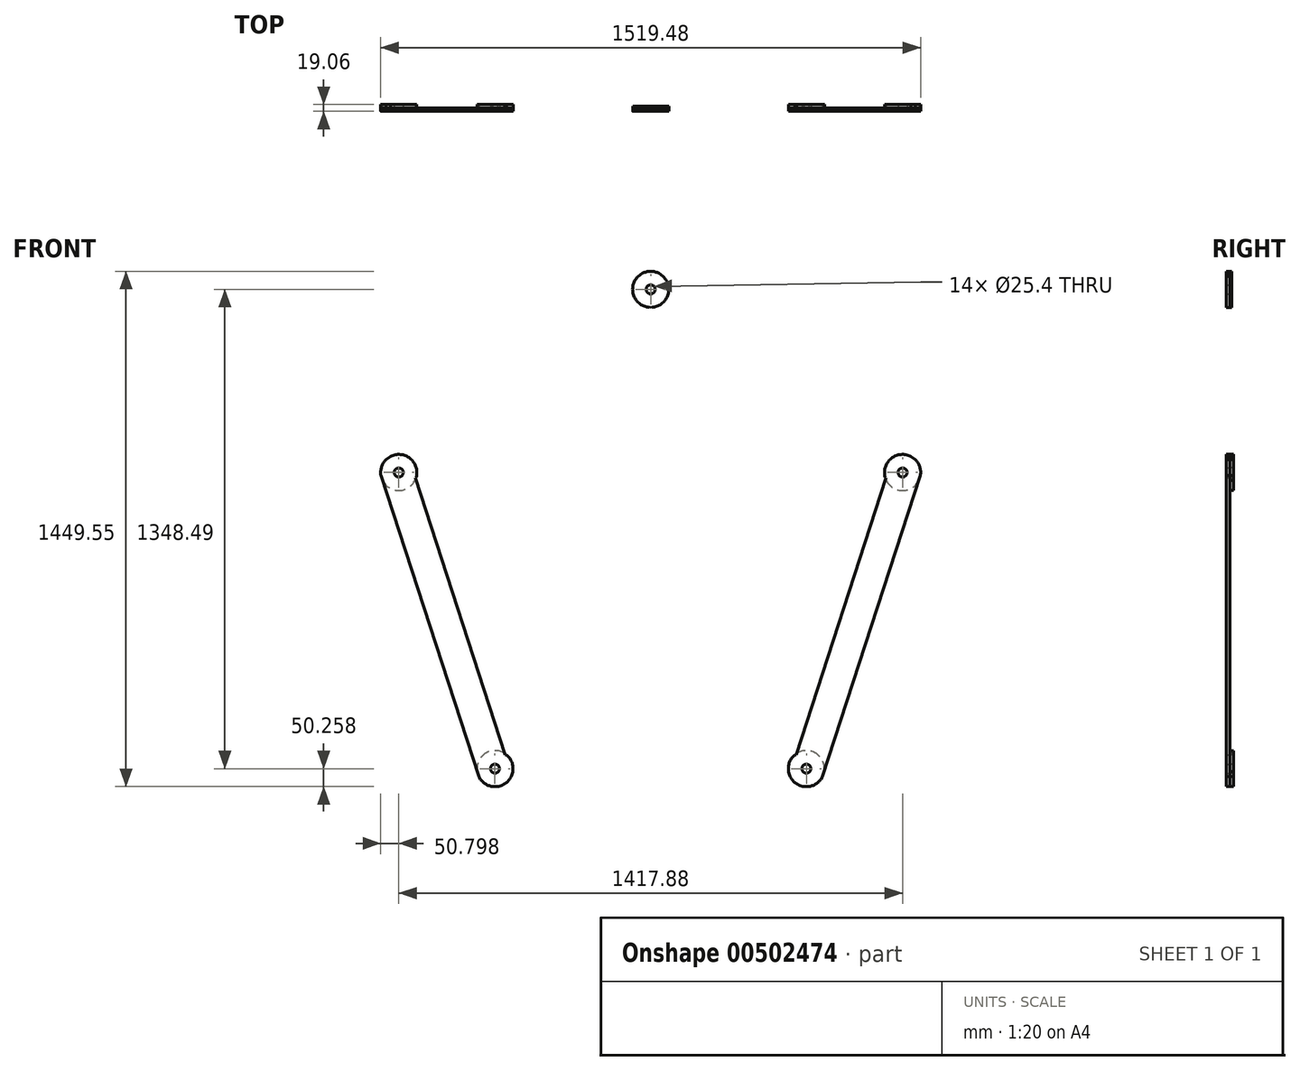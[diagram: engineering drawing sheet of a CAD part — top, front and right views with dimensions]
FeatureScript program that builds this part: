
annotation { "Feature Type Name" : "Feature", "Feature Type Description" : "" }
export const myFeature = defineFeature(function(context is Context, id is Id, definition is map)
    precondition{}
    {
        {
            var Q0;
            Q0=qCreatedBy(makeId("Front.planeOp"),FACE);
            var sketch = newSketch(context, id + "F0", { "sketchPlane" : qUnion([Q0])});
            skCircle(sketch, "E0.cCircle", {"center": v(0, 0) * mm, "radius": 603.06 * mm, "construction": true});
            skLineSegment(sketch, "E0.0", {"start": v(438.15, -603.06) * mm, "end": v(-438.15, -603.06) * mm, "construction": true});
            skLineSegment(sketch, "E0.1", {"start": v(-438.15, -603.06) * mm, "end": v(-708.94, 230.35) * mm, "construction": true});
            skLineSegment(sketch, "E0.2", {"start": v(-708.94, 230.35) * mm, "end": v(0, 745.43) * mm, "construction": true});
            skLineSegment(sketch, "E0.3", {"start": v(0, 745.43) * mm, "end": v(708.94, 230.35) * mm, "construction": true});
            skLineSegment(sketch, "E0.4", {"start": v(708.94, 230.35) * mm, "end": v(438.15, -603.06) * mm, "construction": true});
            skPoint(sketch, "E0.0.midPoint", {"position": v(0, -603.06) * mm});
            skCircle(sketch, "E1", {"center": v(708.94, 230.35) * mm, "radius": 50.8 * mm});
            skCircle(sketch, "E2", {"center": v(708.94, 230.35) * mm, "radius": 12.7 * mm});
            skCircle(sketch, "E3", {"center": v(-708.94, 230.35) * mm, "radius": 50.8 * mm});
            skCircle(sketch, "E4", {"center": v(-708.94, 230.35) * mm, "radius": 12.7 * mm});
            skCircle(sketch, "E5", {"center": v(0, 745.43) * mm, "radius": 50.8 * mm});
            skCircle(sketch, "E6", {"center": v(0, 745.43) * mm, "radius": 12.7 * mm});
            skCircle(sketch, "E7", {"center": v(-438.15, -603.06) * mm, "radius": 50.8 * mm});
            skCircle(sketch, "E8", {"center": v(-438.15, -603.06) * mm, "radius": 12.7 * mm});
            skCircle(sketch, "E9", {"center": v(438.15, -603.06) * mm, "radius": 50.8 * mm});
            skCircle(sketch, "E10", {"center": v(438.15, -603.06) * mm, "radius": 12.7 * mm});
            skCircle(sketch, "E11.cCircle", {"center": v(0, 0) * mm, "radius": 653.32 * mm, "construction": true});
            skLineSegment(sketch, "E11.0", {"start": v(474.66, -653.32) * mm, "end": v(-474.66, -653.32) * mm});
            skLineSegment(sketch, "E11.1", {"start": v(-474.66, -653.32) * mm, "end": v(-768.02, 249.54) * mm});
            skLineSegment(sketch, "E11.2", {"start": v(-768.02, 249.54) * mm, "end": v(0, 807.54) * mm});
            skLineSegment(sketch, "E11.3", {"start": v(0, 807.54) * mm, "end": v(768.02, 249.54) * mm});
            skLineSegment(sketch, "E11.4", {"start": v(768.02, 249.54) * mm, "end": v(474.66, -653.32) * mm});
            skPoint(sketch, "E11.0.midPoint", {"position": v(0, -653.32) * mm});
            skCircle(sketch, "E12.cCircle", {"center": v(0, 0) * mm, "radius": 563.73 * mm, "construction": true});
            skLineSegment(sketch, "E12.0", {"start": v(409.57, -563.73) * mm, "end": v(-409.57, -563.73) * mm});
            skLineSegment(sketch, "E12.1", {"start": v(-409.58, -563.73) * mm, "end": v(-662.7, 215.33) * mm});
            skLineSegment(sketch, "E12.2", {"start": v(-662.7, 215.33) * mm, "end": v(0, 696.81) * mm});
            skLineSegment(sketch, "E12.3", {"start": v(0, 696.81) * mm, "end": v(662.7, 215.33) * mm});
            skLineSegment(sketch, "E12.4", {"start": v(662.7, 215.33) * mm, "end": v(409.58, -563.73) * mm});
            skPoint(sketch, "E12.0.midPoint", {"position": v(0, -563.73) * mm});
            skLineSegment(sketch, "E13", {"start": v(-224.42, -563.73) * mm, "end": v(0, -563.73) * mm});
            skLineSegment(sketch, "E14", {"start": v(0, -653.32) * mm, "end": v(0, -563.73) * mm});
            skSolve(sketch);
        }
        {
            var Q0;
            {var subQ0=sQuery(id+"F0.wireOp",EDGE,"E11.4");var subQ1=sQuery(id+"F0.wireOp",EDGE,"E1");var subQ2=makeQuery(id+"F0.imprint","INTERSECT",VERTEX,{"disambiguationData":[OD(0.0)],"derivedFrom":[subQ1,subQ0]});Q0=makeQuery(id+"F0.imprint","IMPRINT",FACE,{"disambiguationData":[TD([[makeQuery(id+"F0.imprint","IMPRINT",EDGE,{"disambiguationData":[TD([[subQ2,1.0]])],"derivedFrom":subQ1}),-1.0]])]});}
            var Q1;
            Q1=makeQuery(id+"F0.imprint","IMPRINT",FACE,{"disambiguationData":[TD([[makeQuery(id+"F0.imprint","IMPRINT",EDGE,{"derivedFrom":sQuery(id+"F0.wireOp",EDGE,"E2")}),-1.0]])]});
            var Q2;
            {var subQ0=sQuery(id+"F0.wireOp",EDGE,"E11.3");var subQ1=sQuery(id+"F0.wireOp",EDGE,"E1");var subQ2=makeQuery(id+"F0.imprint","INTERSECT",VERTEX,{"disambiguationData":[OD(0.0)],"derivedFrom":[subQ1,subQ0]});Q2=makeQuery(id+"F0.imprint","IMPRINT",FACE,{"disambiguationData":[TD([[makeQuery(id+"F0.imprint","IMPRINT",EDGE,{"disambiguationData":[TD([[subQ2,-1.0]])],"derivedFrom":subQ1}),-1.0]])]});}
            var Q3;
            Q3=makeQuery(id+"F0.imprint","IMPRINT",FACE,{"disambiguationData":[TD([[makeQuery(id+"F0.imprint","IMPRINT",EDGE,{"derivedFrom":sQuery(id+"F0.wireOp",EDGE,"E6")}),-1.0]])]});
            var Q4;
            {var subQ0=sQuery(id+"F0.wireOp",EDGE,"E11.2");var subQ1=sQuery(id+"F0.wireOp",EDGE,"E3");var subQ2=makeQuery(id+"F0.imprint","INTERSECT",VERTEX,{"disambiguationData":[OD(1.0)],"derivedFrom":[subQ1,subQ0]});Q4=makeQuery(id+"F0.imprint","IMPRINT",FACE,{"disambiguationData":[TD([[makeQuery(id+"F0.imprint","IMPRINT",EDGE,{"disambiguationData":[TD([[subQ2,1.0]])],"derivedFrom":subQ1}),-1.0]])]});}
            var Q5;
            Q5=makeQuery(id+"F0.imprint","IMPRINT",FACE,{"disambiguationData":[TD([[makeQuery(id+"F0.imprint","IMPRINT",EDGE,{"derivedFrom":sQuery(id+"F0.wireOp",EDGE,"E4")}),-1.0]])]});
            var Q6;
            {var subQ0=sQuery(id+"F0.wireOp",EDGE,"E11.1");var subQ1=sQuery(id+"F0.wireOp",EDGE,"E3");var subQ2=makeQuery(id+"F0.imprint","INTERSECT",VERTEX,{"disambiguationData":[OD(1.0)],"derivedFrom":[subQ1,subQ0]});Q6=makeQuery(id+"F0.imprint","IMPRINT",FACE,{"disambiguationData":[TD([[makeQuery(id+"F0.imprint","IMPRINT",EDGE,{"disambiguationData":[TD([[subQ2,-1.0]])],"derivedFrom":subQ1}),-1.0]])]});}
            var Q7;
            {var subQ0=sQuery(id+"F0.wireOp",EDGE,"E11.0");var subQ1=sQuery(id+"F0.wireOp",EDGE,"E7");var subQ2=makeQuery(id+"F0.imprint","INTERSECT",VERTEX,{"disambiguationData":[OD(1.0)],"derivedFrom":[subQ1,subQ0]});Q7=makeQuery(id+"F0.imprint","IMPRINT",FACE,{"disambiguationData":[TD([[makeQuery(id+"F0.imprint","IMPRINT",EDGE,{"disambiguationData":[TD([[subQ2,-1.0]])],"derivedFrom":subQ1}),-1.0]])]});}
            var Q8;
            Q8=makeQuery(id+"F0.imprint","IMPRINT",FACE,{"disambiguationData":[TD([[makeQuery(id+"F0.imprint","IMPRINT",EDGE,{"derivedFrom":sQuery(id+"F0.wireOp",EDGE,"E8")}),-1.0]])]});
            var Q9;
            Q9=makeQuery(id+"F0.imprint","IMPRINT",FACE,{"disambiguationData":[TD([[makeQuery(id+"F0.imprint","IMPRINT",EDGE,{"derivedFrom":sQuery(id+"F0.wireOp",EDGE,"E10")}),-1.0]])]});
            extrude(context, id + "F1", {"entities" : qUnion([Q0, Q1, Q2, Q3, Q4, Q5, Q6, Q7, Q8, Q9]), "depth" : 9.52 * mm});
        }
        {
            var Q0;
            Q0=makeQuery(id+"F0.imprint","IMPRINT",FACE,{"disambiguationData":[TD([[makeQuery(id+"F0.imprint","IMPRINT",EDGE,{"derivedFrom":sQuery(id+"F0.wireOp",EDGE,"E2")}),-1.0]])]});
            var Q1;
            {var subQ0=sQuery(id+"F0.wireOp",EDGE,"E11.4");var subQ1=sQuery(id+"F0.wireOp",EDGE,"E1");var subQ2=makeQuery(id+"F0.imprint","INTERSECT",VERTEX,{"disambiguationData":[OD(0.0)],"derivedFrom":[subQ1,subQ0]});Q1=makeQuery(id+"F0.imprint","IMPRINT",FACE,{"disambiguationData":[TD([[makeQuery(id+"F0.imprint","IMPRINT",EDGE,{"disambiguationData":[TD([[subQ2,1.0]])],"derivedFrom":subQ1}),-1.0]])]});}
            var Q2;
            Q2=makeQuery(id+"F0.imprint","IMPRINT",FACE,{"disambiguationData":[TD([[makeQuery(id+"F0.imprint","IMPRINT",EDGE,{"derivedFrom":sQuery(id+"F0.wireOp",EDGE,"E10")}),-1.0]])]});
            var Q3;
            Q3=makeQuery(id+"F0.imprint","IMPRINT",FACE,{"disambiguationData":[TD([[makeQuery(id+"F0.imprint","IMPRINT",EDGE,{"derivedFrom":sQuery(id+"F0.wireOp",EDGE,"E8")}),-1.0]])]});
            var Q4;
            {var subQ0=sQuery(id+"F0.wireOp",EDGE,"E11.1");var subQ1=sQuery(id+"F0.wireOp",EDGE,"E3");var subQ2=makeQuery(id+"F0.imprint","INTERSECT",VERTEX,{"disambiguationData":[OD(1.0)],"derivedFrom":[subQ1,subQ0]});Q4=makeQuery(id+"F0.imprint","IMPRINT",FACE,{"disambiguationData":[TD([[makeQuery(id+"F0.imprint","IMPRINT",EDGE,{"disambiguationData":[TD([[subQ2,-1.0]])],"derivedFrom":subQ1}),-1.0]])]});}
            var Q5;
            Q5=makeQuery(id+"F0.imprint","IMPRINT",FACE,{"disambiguationData":[TD([[makeQuery(id+"F0.imprint","IMPRINT",EDGE,{"derivedFrom":sQuery(id+"F0.wireOp",EDGE,"E4")}),-1.0]])]});
            extrude(context, id + "F2", {"entities" : qUnion([Q0, Q1, Q2, Q3, Q4, Q5]), "depth" : 9.52 * mm});
        }
        {
            var Q0;
            Q0=makeQuery(id+"F0.imprint","IMPRINT",FACE,{"disambiguationData":[TD([[makeQuery(id+"F0.imprint","IMPRINT",EDGE,{"derivedFrom":sQuery(id+"F0.wireOp",EDGE,"E8")}),-1.0]])]});
            var Q1;
            {var subQ0=sQuery(id+"F0.wireOp",EDGE,"E11.0");var subQ1=sQuery(id+"F0.wireOp",EDGE,"E7");var subQ2=makeQuery(id+"F0.imprint","INTERSECT",VERTEX,{"disambiguationData":[OD(1.0)],"derivedFrom":[subQ1,subQ0]});Q1=makeQuery(id+"F0.imprint","IMPRINT",FACE,{"disambiguationData":[TD([[makeQuery(id+"F0.imprint","IMPRINT",EDGE,{"disambiguationData":[TD([[subQ2,-1.0]])],"derivedFrom":subQ1}),-1.0]])]});}
            var Q2;
            Q2=makeQuery(id+"F0.imprint","IMPRINT",FACE,{"disambiguationData":[TD([[makeQuery(id+"F0.imprint","IMPRINT",EDGE,{"derivedFrom":sQuery(id+"F0.wireOp",EDGE,"E10")}),-1.0]])]});
            var Q3;
            {var subQ0=sQuery(id+"F0.wireOp",EDGE,"E11.2");var subQ1=sQuery(id+"F0.wireOp",EDGE,"E3");var subQ2=makeQuery(id+"F0.imprint","INTERSECT",VERTEX,{"disambiguationData":[OD(1.0)],"derivedFrom":[subQ1,subQ0]});Q3=makeQuery(id+"F0.imprint","IMPRINT",FACE,{"disambiguationData":[TD([[makeQuery(id+"F0.imprint","IMPRINT",EDGE,{"disambiguationData":[TD([[subQ2,1.0]])],"derivedFrom":subQ1}),-1.0]])]});}
            var Q4;
            Q4=makeQuery(id+"F0.imprint","IMPRINT",FACE,{"disambiguationData":[TD([[makeQuery(id+"F0.imprint","IMPRINT",EDGE,{"derivedFrom":sQuery(id+"F0.wireOp",EDGE,"E4")}),-1.0]])]});
            var Q5;
            Q5=makeQuery(id+"F0.imprint","IMPRINT",FACE,{"disambiguationData":[TD([[makeQuery(id+"F0.imprint","IMPRINT",EDGE,{"derivedFrom":sQuery(id+"F0.wireOp",EDGE,"E6")}),-1.0]])]});
            extrude(context, id + "F3", {"entities" : qUnion([Q0, Q1, Q2, Q3, Q4, Q5]), "oppositeDirection" : true, "depth" : 9.52 * mm});
        }
        {
            var Q0;
            Q0=makeQuery(id+"F0.imprint","IMPRINT",FACE,{"disambiguationData":[TD([[makeQuery(id+"F0.imprint","IMPRINT",EDGE,{"derivedFrom":sQuery(id+"F0.wireOp",EDGE,"E6")}),-1.0]])]});
            extrude(context, id + "F4", {"entities" : qUnion([Q0]), "operationType" : NewBodyOperationType.REMOVE, "oppositeDirection" : true, "depth" : 4.76 * mm});
        }
        {
            var Q0;
            Q0=makeQuery(id+"F0.imprint","IMPRINT",FACE,{"disambiguationData":[TD([[makeQuery(id+"F0.imprint","IMPRINT",EDGE,{"derivedFrom":sQuery(id+"F0.wireOp",EDGE,"E2")}),-1.0]])]});
            var Q1;
            {var subQ0=sQuery(id+"F0.wireOp",EDGE,"E11.3");var subQ1=sQuery(id+"F0.wireOp",EDGE,"E1");var subQ2=makeQuery(id+"F0.imprint","INTERSECT",VERTEX,{"disambiguationData":[OD(0.0)],"derivedFrom":[subQ1,subQ0]});Q1=makeQuery(id+"F0.imprint","IMPRINT",FACE,{"disambiguationData":[TD([[makeQuery(id+"F0.imprint","IMPRINT",EDGE,{"disambiguationData":[TD([[subQ2,-1.0]])],"derivedFrom":subQ1}),-1.0]])]});}
            var Q2;
            Q2=makeQuery(id+"F0.imprint","IMPRINT",FACE,{"disambiguationData":[TD([[makeQuery(id+"F0.imprint","IMPRINT",EDGE,{"derivedFrom":sQuery(id+"F0.wireOp",EDGE,"E6")}),-1.0]])]});
            extrude(context, id + "F5", {"entities" : qUnion([Q0, Q1, Q2]), "oppositeDirection" : true, "depth" : 9.52 * mm});
        }
        {
            var Q0;
            Q0=makeQuery(id+"F0.imprint","IMPRINT",FACE,{"disambiguationData":[TD([[makeQuery(id+"F0.imprint","IMPRINT",EDGE,{"derivedFrom":sQuery(id+"F0.wireOp",EDGE,"E6")}),-1.0]])]});
            extrude(context, id + "F6", {"entities" : qUnion([Q0]), "operationType" : NewBodyOperationType.REMOVE, "oppositeDirection" : true, "depth" : 9.52 * mm, "hasSecondDirection" : true, "secondDirectionOppositeDirection" : true, "secondDirectionDepth" : 4.76 * mm});
        }
    });
